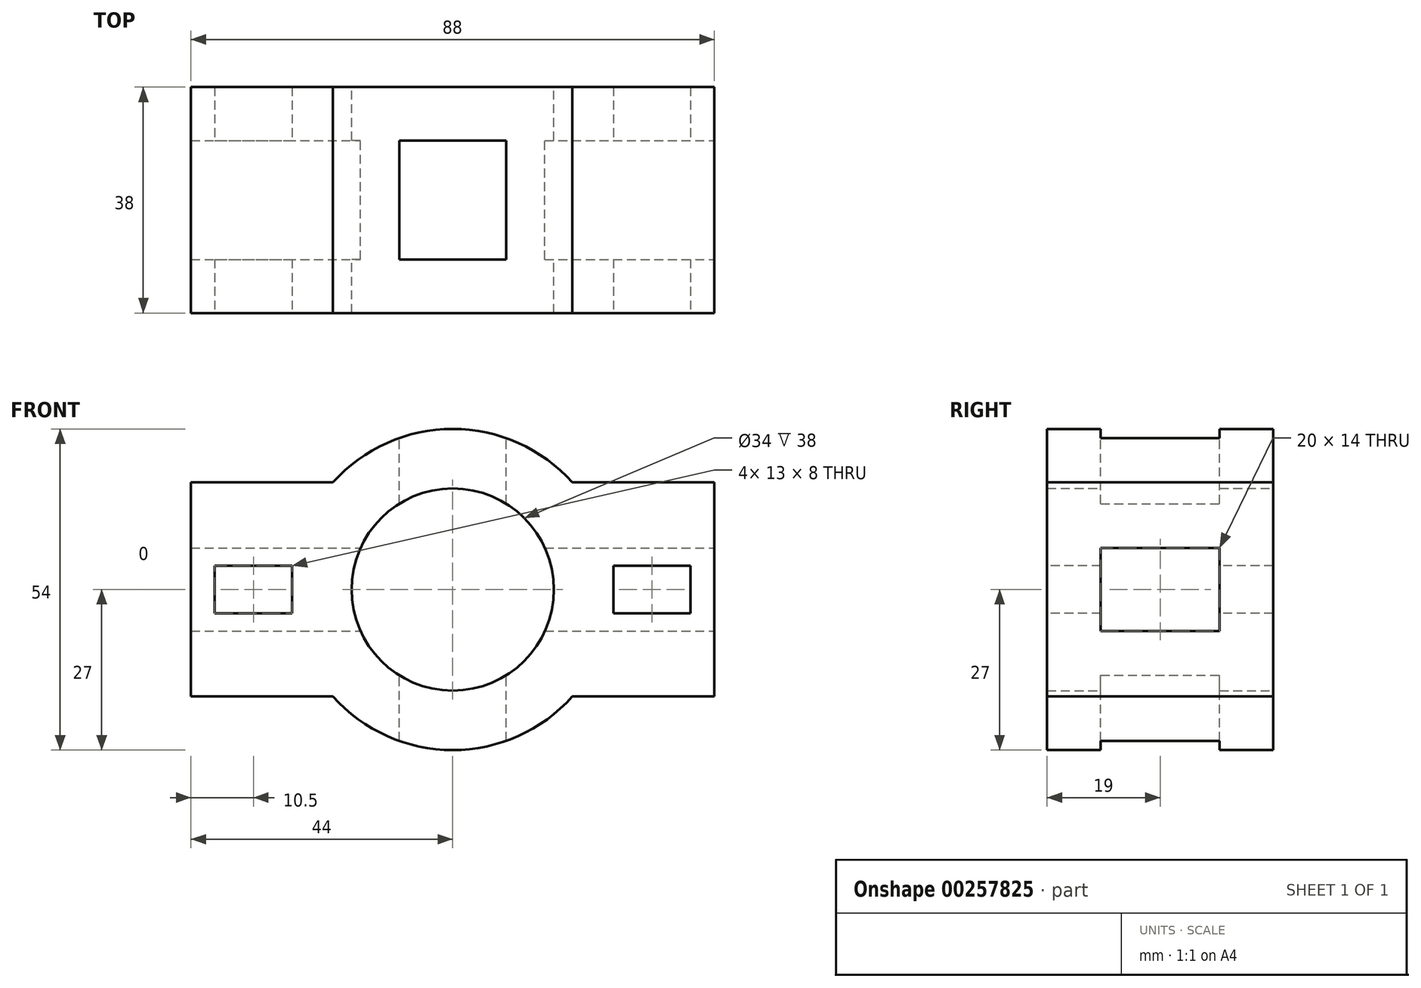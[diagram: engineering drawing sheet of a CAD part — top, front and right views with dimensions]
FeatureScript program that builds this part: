
annotation { "Feature Type Name" : "Feature", "Feature Type Description" : "" }
export const myFeature = defineFeature(function(context is Context, id is Id, definition is map)
    precondition{}
    {
        {
            var Q0;
            Q0=qCreatedBy(makeId("Front.planeOp"),FACE);
            var sketch = newSketch(context, id + "F0", { "sketchPlane" : qUnion([Q0])});
            skCircle(sketch, "E0", {"center": v(0, 0) * mm, "radius": 27 * mm});
            skLineSegment(sketch, "E1.bottom", {"start": v(-20.12, 18) * mm, "end": v(-44, 18) * mm});
            skLineSegment(sketch, "E1.top", {"start": v(-20.12, -18) * mm, "end": v(-44, -18) * mm});
            skLineSegment(sketch, "E1.left", {"start": v(-20.12, 18) * mm, "end": v(-20.12, -18) * mm});
            skLineSegment(sketch, "E1.right", {"start": v(-44, 18) * mm, "end": v(-44, -18) * mm});
            skLineSegment(sketch, "E2.bottom", {"start": v(20.12, 18) * mm, "end": v(44, 18) * mm});
            skLineSegment(sketch, "E2.top", {"start": v(20.12, -18) * mm, "end": v(44, -18) * mm});
            skLineSegment(sketch, "E2.left", {"start": v(20.12, 18) * mm, "end": v(20.12, -18) * mm});
            skLineSegment(sketch, "E2.right", {"start": v(44, 18) * mm, "end": v(44, -18) * mm});
            skCircle(sketch, "E3", {"center": v(0, 0) * mm, "radius": 17 * mm});
            skSolve(sketch);
        }
        {
            var Q0;
            {var subQ1=sQuery(id+"F0.wireOp",EDGE,"E1.bottom");Q0=makeQuery(id+"F0.imprint","IMPRINT",FACE,{"disambiguationData":[TD([[makeQuery(id+"F0.imprint","IMPRINT",EDGE,{"derivedFrom":subQ1}),1.0]])]});}
            var Q1;
            {var subQ0=sQuery(id+"F0.wireOp",EDGE,"E1.left");Q1=makeQuery(id+"F0.imprint","IMPRINT",FACE,{"disambiguationData":[TD([[makeQuery(id+"F0.imprint","IMPRINT",EDGE,{"derivedFrom":subQ0}),-1.0]])]});}
            var Q2;
            {var subQ1=sQuery(id+"F0.wireOp",EDGE,"E1.left");Q2=makeQuery(id+"F0.imprint","IMPRINT",FACE,{"disambiguationData":[TD([[makeQuery(id+"F0.imprint","IMPRINT",EDGE,{"derivedFrom":subQ1}),1.0]])]});}
            var Q3;
            {var subQ0=sQuery(id+"F0.wireOp",EDGE,"E2.left");Q3=makeQuery(id+"F0.imprint","IMPRINT",FACE,{"disambiguationData":[TD([[makeQuery(id+"F0.imprint","IMPRINT",EDGE,{"derivedFrom":subQ0}),1.0]])]});}
            var Q4;
            {var subQ1=sQuery(id+"F0.wireOp",EDGE,"E2.bottom");Q4=makeQuery(id+"F0.imprint","IMPRINT",FACE,{"disambiguationData":[TD([[makeQuery(id+"F0.imprint","IMPRINT",EDGE,{"derivedFrom":subQ1}),-1.0]])]});}
            extrude(context, id + "F1", {"entities" : qUnion([Q0, Q1, Q2, Q3, Q4]), "endBound" : BoundingType.SYMMETRIC, "depth" : 38 * mm});
        }
        {
            var Q0;
            Q0=makeQuery(id+"F1.opExtrude","SWEPT_FACE",FACE,{"disambiguationData":[OSD([sQuery(id+"F0.wireOp",EDGE,"E2.right")])]});
            var sketch = newSketch(context, id + "F2", { "sketchPlane" : qUnion([Q0])});
            skLineSegment(sketch, "E4.bottom", {"start": v(-10, 7) * mm, "end": v(10, 7) * mm});
            skLineSegment(sketch, "E4.top", {"start": v(-10, -7) * mm, "end": v(10, -7) * mm});
            skLineSegment(sketch, "E4.left", {"start": v(-10, 7) * mm, "end": v(-10, -7) * mm});
            skLineSegment(sketch, "E4.right", {"start": v(10, 7) * mm, "end": v(10, -7) * mm});
            skSolve(sketch);
        }
        {
            var Q0;
            Q0 = qSketchRegion(id + "F2", true);
            extrude(context, id + "F3", {"entities" : qUnion([Q0]), "operationType" : NewBodyOperationType.REMOVE, "endBound" : BoundingType.THROUGH_ALL, "oppositeDirection" : true, "depth" : 25 * mm});
        }
        {
            var Q0;
            Q0=makeQuery(id+"F1.opExtrude","CAP_FACE",FACE,{"disambiguationData":[OSD([sQuery(id+"F0.wireOp",EDGE,"E0"),sQuery(id+"F0.wireOp",EDGE,"E1.bottom"),sQuery(id+"F0.wireOp",EDGE,"E1.top"),sQuery(id+"F0.wireOp",EDGE,"E1.right"),sQuery(id+"F0.wireOp",EDGE,"E2.bottom"),sQuery(id+"F0.wireOp",EDGE,"E2.top"),sQuery(id+"F0.wireOp",EDGE,"E2.right"),sQuery(id+"F0.wireOp",EDGE,"E3")])],"isStart":false});
            var sketch = newSketch(context, id + "F4", { "sketchPlane" : qUnion([Q0])});
            skLineSegment(sketch, "E5.bottom", {"start": v(-40, 4) * mm, "end": v(-27, 4) * mm});
            skLineSegment(sketch, "E5.top", {"start": v(-40, -4) * mm, "end": v(-27, -4) * mm});
            skLineSegment(sketch, "E5.left", {"start": v(-40, 4) * mm, "end": v(-40, -4) * mm});
            skLineSegment(sketch, "E5.right", {"start": v(-27, 4) * mm, "end": v(-27, -4) * mm});
            skLineSegment(sketch, "E6.bottom", {"start": v(27, 4) * mm, "end": v(40, 4) * mm});
            skLineSegment(sketch, "E6.top", {"start": v(27, -4) * mm, "end": v(40, -4) * mm});
            skLineSegment(sketch, "E6.left", {"start": v(27, 4) * mm, "end": v(27, -4) * mm});
            skLineSegment(sketch, "E6.right", {"start": v(40, 4) * mm, "end": v(40, -4) * mm});
            skSolve(sketch);
        }
        {
            var Q0;
            Q0 = qSketchRegion(id + "F4", true);
            extrude(context, id + "F5", {"entities" : qUnion([Q0]), "operationType" : NewBodyOperationType.REMOVE, "endBound" : BoundingType.THROUGH_ALL, "oppositeDirection" : true, "depth" : 25 * mm});
        }
        {
            var Q0;
            Q0=qCreatedBy(makeId("Top.planeOp"),FACE);
            var sketch = newSketch(context, id + "F6", { "sketchPlane" : qUnion([Q0])});
            skLineSegment(sketch, "E7.bottom", {"start": v(-9, 10) * mm, "end": v(9, 10) * mm});
            skLineSegment(sketch, "E7.top", {"start": v(-9, -10) * mm, "end": v(9, -10) * mm});
            skLineSegment(sketch, "E7.left", {"start": v(-9, 10) * mm, "end": v(-9, -10) * mm});
            skLineSegment(sketch, "E7.right", {"start": v(9, 10) * mm, "end": v(9, -10) * mm});
            skPoint(sketch, "E7.middle", {"position": v(0, 0) * mm});
            skSolve(sketch);
        }
        {
            var Q0;
            Q0 = qSketchRegion(id + "F6", true);
            extrude(context, id + "F7", {"entities" : qUnion([Q0]), "operationType" : NewBodyOperationType.REMOVE, "endBound" : BoundingType.SYMMETRIC, "oppositeDirection" : true, "depth" : 100 * mm});
        }
    });
